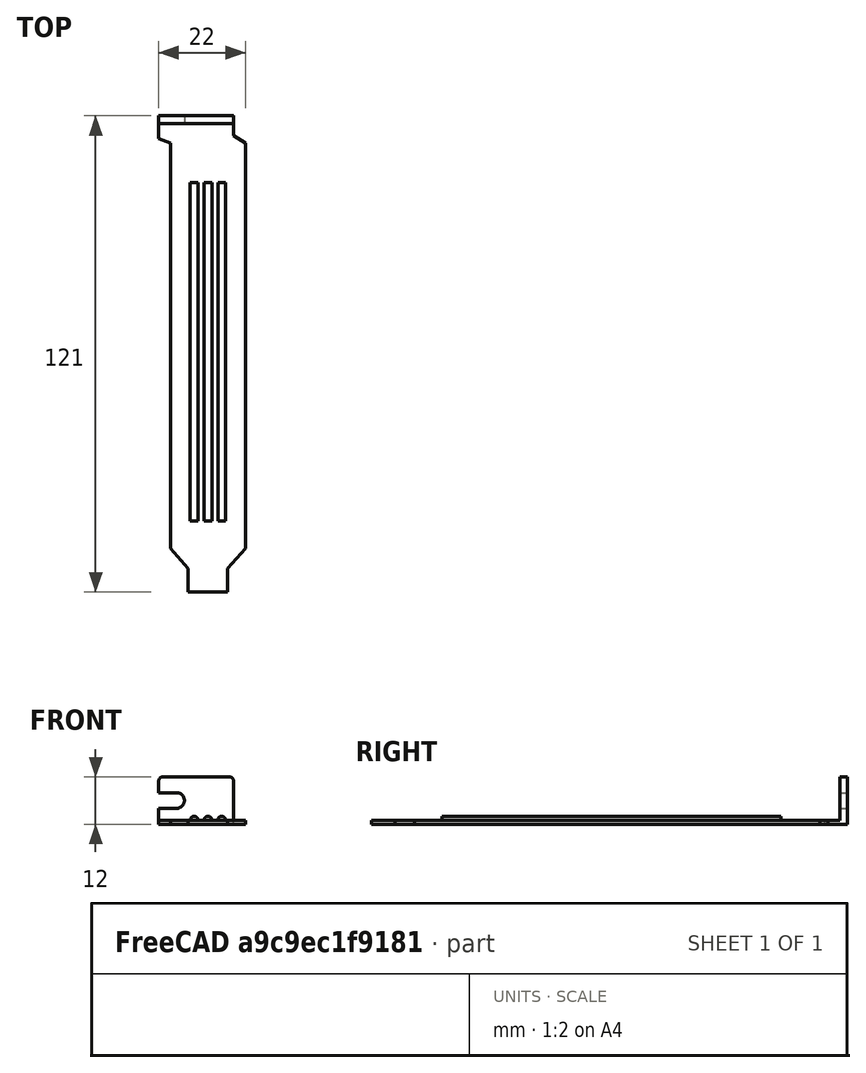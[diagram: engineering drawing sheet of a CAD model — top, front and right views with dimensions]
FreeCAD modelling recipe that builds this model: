
FCSTD DOCUMENT  (FreeCAD 0.18.4R)
Label: EmptyCover
License: All rights reserved
LicenseURL: http://en.wikipedia.org/wiki/All_rights_reserved
objects: PartDesign::SubtractiveWedge×4, PartDesign::AdditiveBox×3, PartDesign::AdditiveCylinder×3, PartDesign::SubtractiveCylinder×1, PartDesign::SubtractiveBox×1, PartDesign::Fillet×1, PartDesign::Body×1
note: 26 computed .brp shape members not serialized (recipe doc carries the construction recipe); baked Part::Feature solids carry a one-line shape summary decoded from their .brp

FEATURE [PartDesign::AdditiveBox] Box
  AttacherType = Attacher::AttachEngine3D
  AttachmentOffset = pos=(-9.5,-60,0) rot=(0,0,1;0rad)
  Height = 1
  Length = 19
  MapMode = 5
  Placement = pos=(-9.5,-60,0) rot=(0,0,1;0rad)
  Refine = true
  Support = -> [XY_Plane]
  Width = 114
FEATURE [PartDesign::SubtractiveWedge] Wedge
  AttacherType = Attacher::AttachEngine3D
  AttachmentOffset = pos=(5,-54,-1) rot=(0,0,-1;1.5708rad)
  BaseFeature = -> Box
  MapMode = 5
  Placement = pos=(5,-54,-1) rot=(0,0,-1;1.5708rad)
  Refine = true
  Support = -> [XY_Plane]
  X2max = 7
  X2min = -5
  Xmax = 7
  Xmin = 0
  Ymax = 4.5
  Ymin = 0
  Z2max = 5
  Z2min = 0
  Zmax = 5
  Zmin = 0
FEATURE [PartDesign::SubtractiveWedge] Wedge001
  AttacherType = Attacher::AttachEngine3D
  AttachmentOffset = pos=(5,-54,-1) rot=(0,0,-1;1.5708rad)
  BaseFeature = -> Wedge
  MapMode = 2
  Placement = pos=(-5,-54,1) rot=(-0.707107,0.707107,0;3.14159rad)
  Refine = true
  Support = -> [XY_Plane]
  X2max = 7
  X2min = -5
  Xmax = 7
  Xmin = 0
  Ymax = 4.5
  Ymin = 0
  Z2max = 5
  Z2min = 0
  Zmax = 5
  Zmin = 0
FEATURE [PartDesign::AdditiveBox] Box001
  AttacherType = Attacher::AttachEngine3D
  AttachmentOffset = pos=(-12.5,54,0) rot=(0,0,1;0rad)
  BaseFeature = -> Wedge001
  Height = 1
  Length = 22
  MapMode = 5
  Placement = pos=(-12.5,54,0) rot=(0,0,1;0rad)
  Refine = true
  Support = -> [XY_Plane]
  Width = 7
FEATURE [PartDesign::SubtractiveWedge] Wedge002
  AttacherType = Attacher::AttachEngine3D
  AttachmentOffset = pos=(6.5,60,0) rot=(0,0,-1;1.5708rad)
  BaseFeature = -> Box001
  MapMode = 5
  Placement = pos=(6.5,60,0) rot=(0,0,-1;1.5708rad)
  Refine = true
  Support = -> [XY_Plane]
  X2max = 6
  X2min = -1
  Xmax = 4
  Xmin = -1
  Ymax = 3
  Ymin = 0
  Z2max = 4
  Z2min = 0
  Zmax = 5
  Zmin = 0
FEATURE [PartDesign::SubtractiveWedge] Wedge003
  AttacherType = Attacher::AttachEngine3D
  AttachmentOffset = pos=(-19.5,54,0) rot=(0,0,1;0rad)
  BaseFeature = -> Wedge002
  MapMode = 5
  Placement = pos=(-19.5,54,0) rot=(0,0,1;0rad)
  Refine = true
  Support = -> [XY_Plane]
  X2max = 5
  X2min = 0
  Xmax = 10
  Xmin = 0
  Ymax = 2
  Ymin = 0
  Z2max = 1
  Z2min = 0
  Zmax = 1
  Zmin = 0
FEATURE [PartDesign::AdditiveBox] Box002
  AttacherType = Attacher::AttachEngine3D
  AttachmentOffset = pos=(-12.5,59,0) rot=(0,0,1;0rad)
  BaseFeature = -> Wedge003
  Height = 12
  Length = 19
  MapMode = 5
  Placement = pos=(-12.5,59,0) rot=(0,0,1;0rad)
  Refine = true
  Support = -> [XY_Plane]
  Width = 2
FEATURE [PartDesign::SubtractiveCylinder] Cylinder
  Angle = 360
  AttacherType = Attacher::AttachEngine3D
  AttachmentOffset = pos=(-8,6,-61) rot=(0,0,1;0rad)
  BaseFeature = -> Box002
  Height = 2
  MapMode = 3
  Placement = pos=(-8,61,6) rot=(1,0,0;1.5708rad)
  Radius = 2
  Refine = true
  Support = -> [XY_Plane]
FEATURE [PartDesign::SubtractiveBox] Box003
  AttacherType = Attacher::AttachEngine3D
  AttachmentOffset = pos=(-13,59,4) rot=(0,0,1;0rad)
  BaseFeature = -> Cylinder
  Height = 4
  Length = 5
  MapMode = 5
  Placement = pos=(-13,59,4) rot=(0,0,1;0rad)
  Refine = true
  Support = -> [XY_Plane]
  Width = 2
FEATURE [PartDesign::Fillet] Fillet
  Base = -> Box003 [Edge46,Edge54]
  BaseFeature = -> Box003
  Placement = pos=(-13,59,4) rot=(0,0,1;0rad)
  Radius = 1
FEATURE [PartDesign::AdditiveCylinder] Cylinder001
  Angle = 180
  AttacherType = Attacher::AttachEngine3D
  AttachmentOffset = pos=(0,1,-44) rot=(0,0,1;0rad)
  BaseFeature = -> Fillet
  Height = 86
  MapMode = 5
  Placement = pos=(0,44,1) rot=(1,0,0;1.5708rad)
  Radius = 1
  Refine = true
  Support = -> [XZ_Plane]
FEATURE [PartDesign::AdditiveCylinder] Cylinder002
  Angle = 180
  AttacherType = Attacher::AttachEngine3D
  AttachmentOffset = pos=(3.5,1,-44) rot=(0,0,1;0rad)
  BaseFeature = -> Cylinder001
  Height = 86
  MapMode = 5
  Placement = pos=(3.5,44,1) rot=(1,0,0;1.5708rad)
  Radius = 1
  Refine = true
  Support = -> [XZ_Plane]
FEATURE [PartDesign::AdditiveCylinder] Cylinder003
  Angle = 180
  AttacherType = Attacher::AttachEngine3D
  AttachmentOffset = pos=(-3.5,1,-44) rot=(0,0,1;0rad)
  BaseFeature = -> Cylinder002
  Height = 86
  MapMode = 5
  Placement = pos=(-3.5,44,1) rot=(1,0,0;1.5708rad)
  Radius = 1
  Refine = true
  Support = -> [XZ_Plane]
FEATURE [PartDesign::Body] Body  label="Amiga-EATX-Slot-Bracket"
  Group = -> [Box,Wedge,Wedge001,Box001,Wedge002,Wedge003,Box002,Cylinder,Box003,Fillet,Cylinder001,Cylinder002,Cylinder003]
  Origin = -> Origin
  Tip = -> Cylinder003
